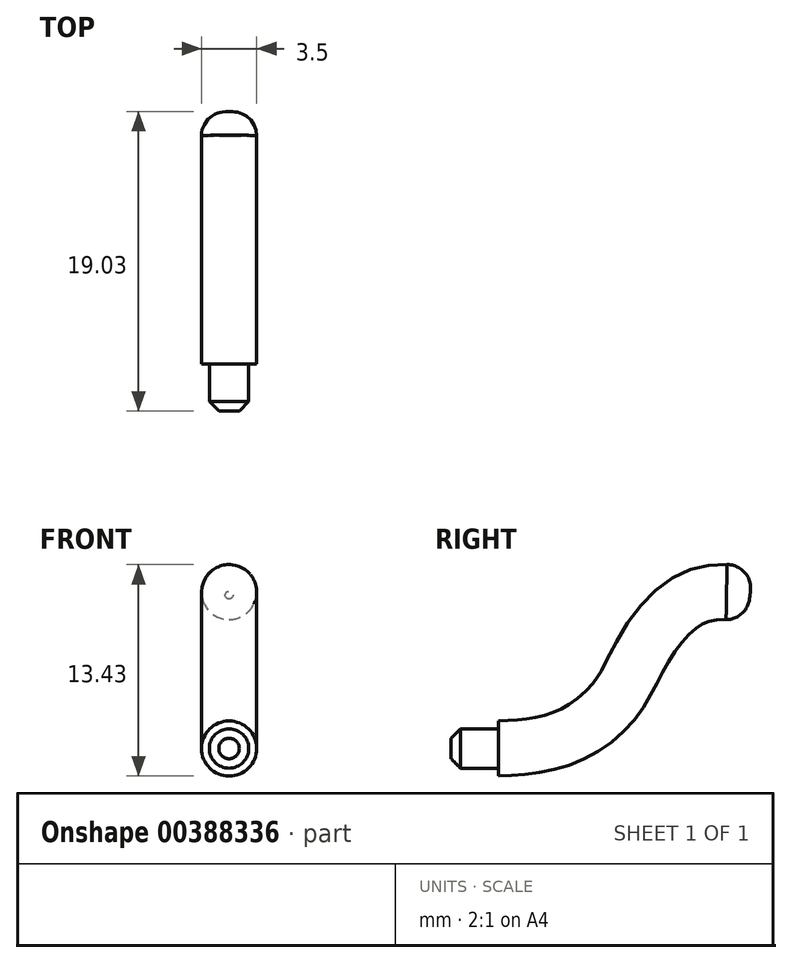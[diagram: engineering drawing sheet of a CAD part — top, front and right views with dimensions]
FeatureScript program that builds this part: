
annotation { "Feature Type Name" : "Feature", "Feature Type Description" : "" }
export const myFeature = defineFeature(function(context is Context, id is Id, definition is map)
    precondition{}
    {
        {
            var Q0;
            Q0=qCreatedBy(makeId("Front.planeOp"),FACE);
            var sketch = newSketch(context, id + "F0", { "sketchPlane" : qUnion([Q0])});
            skCircle(sketch, "E0", {"center": v(0, 0) * mm, "radius": 1.75 * mm});
            skSolve(sketch);
        }
        {
            var Q0;
            Q0=qCreatedBy(makeId("Right.planeOp"),FACE);
            var sketch = newSketch(context, id + "F1", { "sketchPlane" : qUnion([Q0])});
            skFitSpline(sketch, "E1", {"points": [v(0, 0) * mm, v(3.94, 0.6) * mm, v(7.3, 2.94) * mm, v(9.3, 6.4) * mm, v(12.32, 9.53) * mm, v(16, 9.86) * mm], "startDerivative": vector(20.12, 1.1) * mm, "endDerivative": vector(20, -1.46) * mm});
            skSolve(sketch);
        }
        {
            var Q0;
            Q0 = qSketchRegion(id + "F0", true);
            var Q1;
            Q1 = qConstructionFilter(qBodyType(qCreatedBy(id + "F1" ,EDGE), BodyType.WIRE), ConstructionObject.NO);
            sweep(context, id + "F2", {"profiles" : qUnion([Q0]), "path" : qUnion([Q1])});
        }
        {
            var Q0;
            Q0=qCreatedBy(makeId("Front.planeOp"),FACE);
            var sketch = newSketch(context, id + "F3", { "sketchPlane" : qUnion([Q0])});
            skCircle(sketch, "E2", {"center": v(0, 0) * mm, "radius": 1.25 * mm});
            skSolve(sketch);
        }
        {
            var Q0;
            Q0 = qSketchRegion(id + "F3", true);
            extrude(context, id + "F4", {"entities" : qUnion([Q0]), "operationType" : NewBodyOperationType.ADD, "depth" : 3 * mm});
        }
        {
            var Q0;
            Q0=makeQuery(id+"F4.opExtrude","CAP_EDGE",EDGE,{"disambiguationData":[OSD([sQuery(id+"F3.wireOp",EDGE,"E2")])],"isStart":false});
            chamfer(context, id + "F5", {"entities" : qUnion([Q0]), "width" : 0.6 * mm, "tangentPropagation" : true});
        }
        {
            var Q0;
            Q0=makeQuery(id+"F2.opSweep","CAP_EDGE",EDGE,{"disambiguationData":[OSD([sQuery(id+"F0.wireOp",EDGE,"E0"),sQuery(id+"F1.wireOp",VERTEX,"zuPuI0XH-QGrz-46d4-89d8-ainuT5Kvhc82.end")])],"isStart":false});
            fillet(context, id + "F6", {"entities" : qUnion([Q0]), "radius" : 1.5 * mm, "tangentPropagation" : true, "allowEdgeOverflow" : false});
        }
    });
